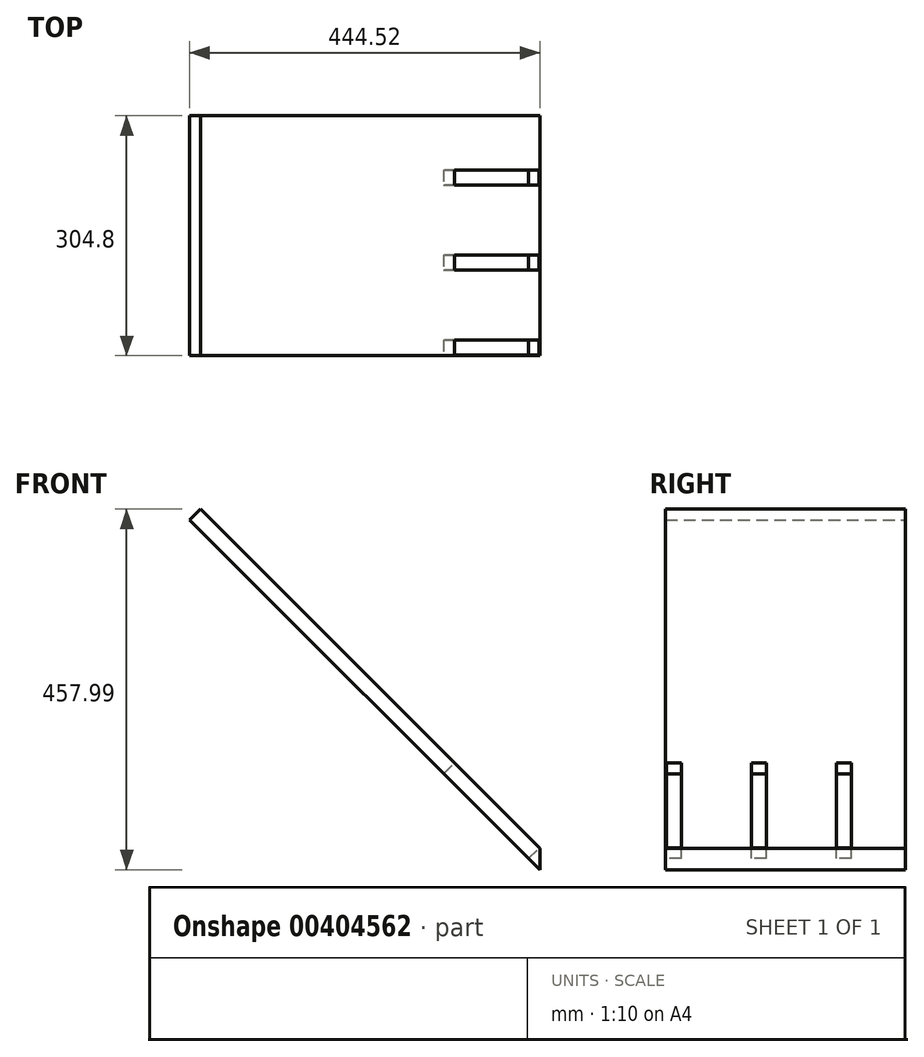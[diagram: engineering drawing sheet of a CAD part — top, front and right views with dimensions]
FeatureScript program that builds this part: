
annotation { "Feature Type Name" : "Feature", "Feature Type Description" : "" }
export const myFeature = defineFeature(function(context is Context, id is Id, definition is map)
    precondition{}
    {
        {
            var Q0;
            Q0=qCreatedBy(makeId("Front.planeOp"),FACE);
            var sketch = newSketch(context, id + "F0", { "sketchPlane" : qUnion([Q0])});
            skLineSegment(sketch, "E0.MirrorCS", {"start": v(378.53, 134.65) * mm, "end": v(-66, 579.17) * mm});
            skLineSegment(sketch, "E1.MirrorCS", {"start": v(378.53, 161.6) * mm, "end": v(-52.52, 592.64) * mm});
            skLineSegment(sketch, "E2.MirrorCS", {"start": v(378.53, 134.65) * mm, "end": v(378.53, 161.6) * mm});
            skLineSegment(sketch, "E3", {"start": v(-52.52, 592.64) * mm, "end": v(-66, 579.17) * mm});
            skSolve(sketch);
        }
        {
            var Q0;
            Q0=qSketchRegion(id+"F0",true);
            extrude(context, id + "F1", {"entities" : qUnion([Q0]), "endBound" : BoundingType.SYMMETRIC, "depth" : 304.8 * mm});
        }
        {
            var Q0;
            Q0=makeQuery(id+"F1.opExtrude","SWEPT_FACE",FACE,{"disambiguationData":[OSD([sQuery(id+"F0.wireOp",EDGE,"E1.MirrorCS")])]});
            var sketch = newSketch(context, id + "F2", { "sketchPlane" : qUnion([Q0])});
            skLineSegment(sketch, "E4.bottom", {"start": v(83.55, -152.4) * mm, "end": v(64.5, -152.4) * mm});
            skLineSegment(sketch, "E4.top", {"start": v(83.55, 0) * mm, "end": v(64.5, 0) * mm});
            skLineSegment(sketch, "E4.left", {"start": v(83.55, -152.4) * mm, "end": v(83.55, 0) * mm});
            skLineSegment(sketch, "E4.right", {"start": v(64.5, -152.4) * mm, "end": v(64.5, 0) * mm});
            skLineSegment(sketch, "E5.bottom", {"start": v(-24.4, -152.4) * mm, "end": v(-43.45, -152.4) * mm});
            skLineSegment(sketch, "E5.top", {"start": v(-24.4, 0) * mm, "end": v(-43.45, 0) * mm});
            skLineSegment(sketch, "E5.left", {"start": v(-24.4, -152.4) * mm, "end": v(-24.4, 0) * mm});
            skLineSegment(sketch, "E5.right", {"start": v(-43.45, -152.4) * mm, "end": v(-43.45, 0) * mm});
            skLineSegment(sketch, "E6.bottom", {"start": v(-132.35, -152.4) * mm, "end": v(-151.4, -152.4) * mm});
            skLineSegment(sketch, "E6.top", {"start": v(-132.35, 0) * mm, "end": v(-151.4, 0) * mm});
            skLineSegment(sketch, "E6.left", {"start": v(-132.35, -152.4) * mm, "end": v(-132.35, 0) * mm});
            skLineSegment(sketch, "E6.right", {"start": v(-151.4, -152.4) * mm, "end": v(-151.4, 0) * mm});
            skLineSegment(sketch, "E7.bottom", {"start": v(-240.3, -152.4) * mm, "end": v(-259.35, -152.4) * mm});
            skLineSegment(sketch, "E7.top", {"start": v(-240.3, 0) * mm, "end": v(-259.35, 0) * mm});
            skLineSegment(sketch, "E7.left", {"start": v(-240.3, -152.4) * mm, "end": v(-240.3, 0) * mm});
            skLineSegment(sketch, "E7.right", {"start": v(-259.35, -152.4) * mm, "end": v(-259.35, 0) * mm});
            skLineSegment(sketch, "E8.bottom", {"start": v(-348.25, -152.4) * mm, "end": v(-367.3, -152.4) * mm});
            skLineSegment(sketch, "E8.top", {"start": v(-348.25, 0) * mm, "end": v(-367.3, 0) * mm});
            skLineSegment(sketch, "E8.left", {"start": v(-348.25, -152.4) * mm, "end": v(-348.25, 0) * mm});
            skLineSegment(sketch, "E8.right", {"start": v(-367.3, -152.4) * mm, "end": v(-367.3, 0) * mm});
            skSolve(sketch);
        }
        {
            var Q0;
            Q0=qSketchRegion(id+"F2",true);
            extrude(context, id + "F3", {"entities" : qUnion([Q0]), "operationType" : NewBodyOperationType.REMOVE, "oppositeDirection" : true, "depth" : 19.05 * mm});
        }
    });
